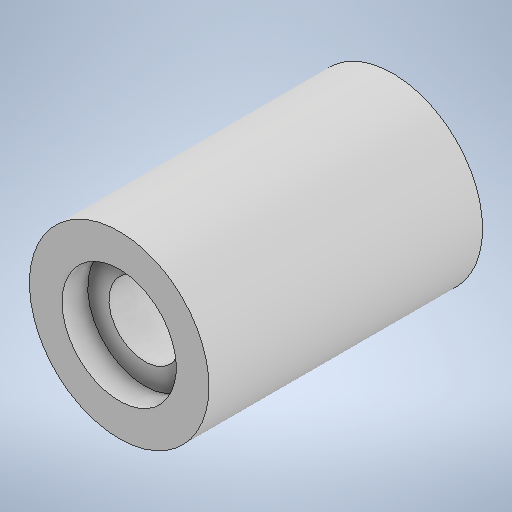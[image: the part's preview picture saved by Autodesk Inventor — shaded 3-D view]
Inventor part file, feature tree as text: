
AUTODESK INVENTOR PART (.ipt)
format: ipt  version: 2025 (Build 290162000, 162)  size: 5,077,504 bytes
history: native  units: mm
features: extrude x5, sketch x5, projected_geometry x4, mirror x2, imported_body x1, plane x1, pattern_circular x1
ambient origin geometry x8: Origin, YZ Plane, XZ Plane, XY Plane, X Axis, Y Axis, Z Axis, Center Point
bodies: Solid1 (feature_tree)
feature tree (19):
  imported_body  "Base1"
  extrude  "Extrusion1"  Depth=10.0mm TaperAngle=0.0deg
  plane  "Work Plane1"
  extrude  "Extrusion2"  Depth=2.0mm
  mirror  "Mirror1"
  extrude  "Extrusion3"  Depth=21.0mm TaperAngle=0.0deg
  mirror  "Mirror2"
  extrude  "Extrusion5"  Depth=35.0mm
  extrude  "Extrusion4"  [1 undecoded]
  pattern_circular  "Circular Pattern1"  [2 undecoded]
  sketch  "Sketch1"  dims[d0=21.0mm d1=0.0mm d2=10.0mm d3=0.0mm]
  projected_geometry  "Projected Loop1"
  sketch  "Sketch2"  dims[d4=0.015mm d5=0.0mm d6=2.0mm]
  sketch  "Sketch3"  dims[d7=5.0mm d8=21.0mm d9=0.0mm]
  projected_geometry  "Projected Loop2"
  sketch  "Sketch4"  dims[d10=80.0mm d11=360.0deg d13=35.0mm]
  projected_geometry  "Projected Loop3"
  sketch  "Sketch5"  dims[d14=0.0mm d15=0.0mm]
  projected_geometry  "Projected Loop4"
note: 3 required parameter values undecoded (feature->parameter linkage not recoverable at this tier; creation-order binding heuristic only, values carry confidence <= 0.55)
